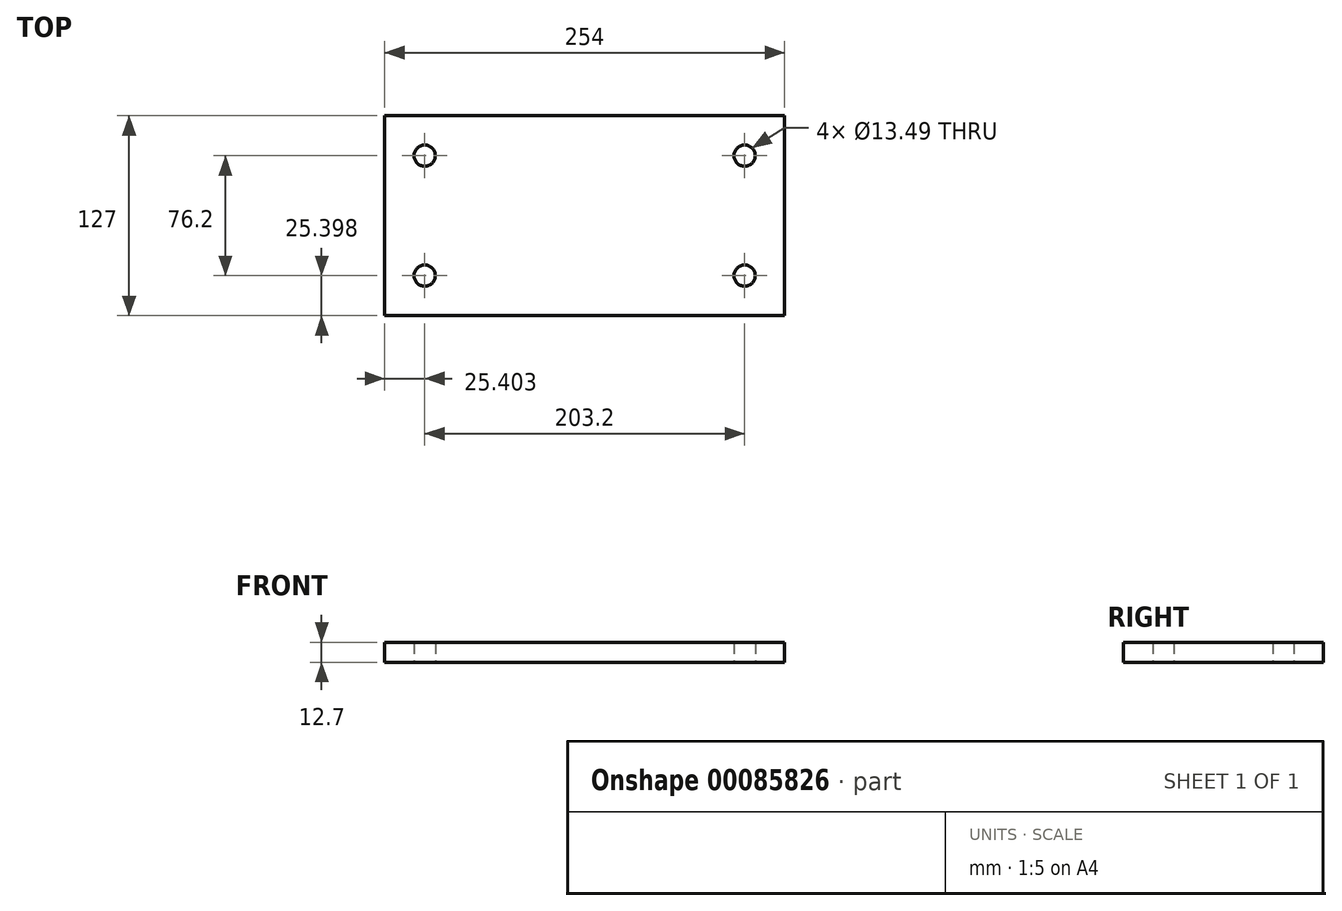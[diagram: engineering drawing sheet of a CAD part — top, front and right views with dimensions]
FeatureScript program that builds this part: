
annotation { "Feature Type Name" : "Feature", "Feature Type Description" : "" }
export const myFeature = defineFeature(function(context is Context, id is Id, definition is map)
    precondition{}
    {
        {
            var Q0;
            Q0=qCreatedBy(makeId("Top.planeOp"),FACE);
            var sketch = newSketch(context, id + "F0", { "sketchPlane" : qUnion([Q0])});
            skLineSegment(sketch, "E0.bottom", {"start": v(116.38, -66.85) * mm, "end": v(-137.62, -66.85) * mm});
            skLineSegment(sketch, "E0.top", {"start": v(116.38, 60.15) * mm, "end": v(-137.62, 60.15) * mm});
            skLineSegment(sketch, "E0.left", {"start": v(116.38, -66.85) * mm, "end": v(116.38, 60.15) * mm});
            skLineSegment(sketch, "E0.right", {"start": v(-137.62, -66.85) * mm, "end": v(-137.62, 60.15) * mm});
            skSolve(sketch);
        }
        {
            var Q0;
            Q0=makeQuery(id+"F0.imprint","IMPRINT",FACE,{"disambiguationData":[TD([[makeQuery(id+"F0.imprint","IMPRINT",EDGE,{"derivedFrom":sQuery(id+"F0.wireOp",EDGE,"E0.bottom")}),-1.0]])]});
            extrude(context, id + "F1", {"entities" : qUnion([Q0]), "depth" : 12.7 * mm, "offsetDistance" : 25.4 * mm});
        }
        {
            var Q0;
            Q0=makeQuery(id+"F1.opExtrude","CAP_FACE",FACE,{"disambiguationData":[OSD([sQuery(id+"F0.wireOp",EDGE,"E0.bottom"),sQuery(id+"F0.wireOp",EDGE,"E0.top"),sQuery(id+"F0.wireOp",EDGE,"E0.left"),sQuery(id+"F0.wireOp",EDGE,"E0.right")])],"isStart":false});
            var sketch = newSketch(context, id + "F2", { "sketchPlane" : qUnion([Q0])});
            skPoint(sketch, "E1", {"position": v(-112.22, 34.75) * mm});
            skLineSegment(sketch, "E2", {"start": v(-10.62, 60.15) * mm, "end": v(-10.62, -66.85) * mm});
            skLineSegment(sketch, "E3", {"start": v(-137.62, -3.35) * mm, "end": v(116.38, -3.35) * mm});
            skPoint(sketch, "E4.MirrorP", {"position": v(90.98, 34.75) * mm});
            skPoint(sketch, "E5.MirrorP", {"position": v(-112.22, -41.45) * mm});
            skPoint(sketch, "E6.MirrorP", {"position": v(90.98, -41.45) * mm});
            skSolve(sketch);
        }
        {
            var Q0;
            Q0=sQuery(id+"F2.wireOp",VERTEX,"E1");
            var Q1;
            Q1=sQuery(id+"F2.wireOp",VERTEX,"E5.MirrorP");
            var Q2;
            Q2=sQuery(id+"F2.wireOp",VERTEX,"E4.MirrorP");
            var Q3;
            Q3=sQuery(id+"F2.wireOp",VERTEX,"E6.MirrorP");
            var Q4;
            Q4=makeQuery(id+"F1.opExtrude","SWEPT_BODY",BODY,{"disambiguationData":[OSD([sQuery(id+"F0.wireOp",EDGE,"E0.bottom"),sQuery(id+"F0.wireOp",EDGE,"E0.top"),sQuery(id+"F0.wireOp",EDGE,"E0.left"),sQuery(id+"F0.wireOp",EDGE,"E0.right")])]});
            hole(context, id + "F3", {"style" : HoleStyle.SIMPLE, "endStyle" : HoleEndStyle.THROUGH, "standardTappedOrClearance" : lookupTablePath({ "standard" : "ANSI", "fit" : "Normal (ASME)", "size" : "1/2", "type" : "Clearance" }), "standardBlindInLast" : lookupTablePath({ "fit" : "Free", "standard" : "ANSI", "size" : "1/2", "type" : "Clearance" }), "holeDiameter" : 13.5 * mm, "majorDiameter" : 12.7 * mm, "isTappedThrough" : true, "tappedDepth" : 12.7 * mm, "tapClearance" : 3, "locations" : qUnion([Q0, Q1, Q2, Q3]), "scope" : qUnion([Q4])});
        }
    });
